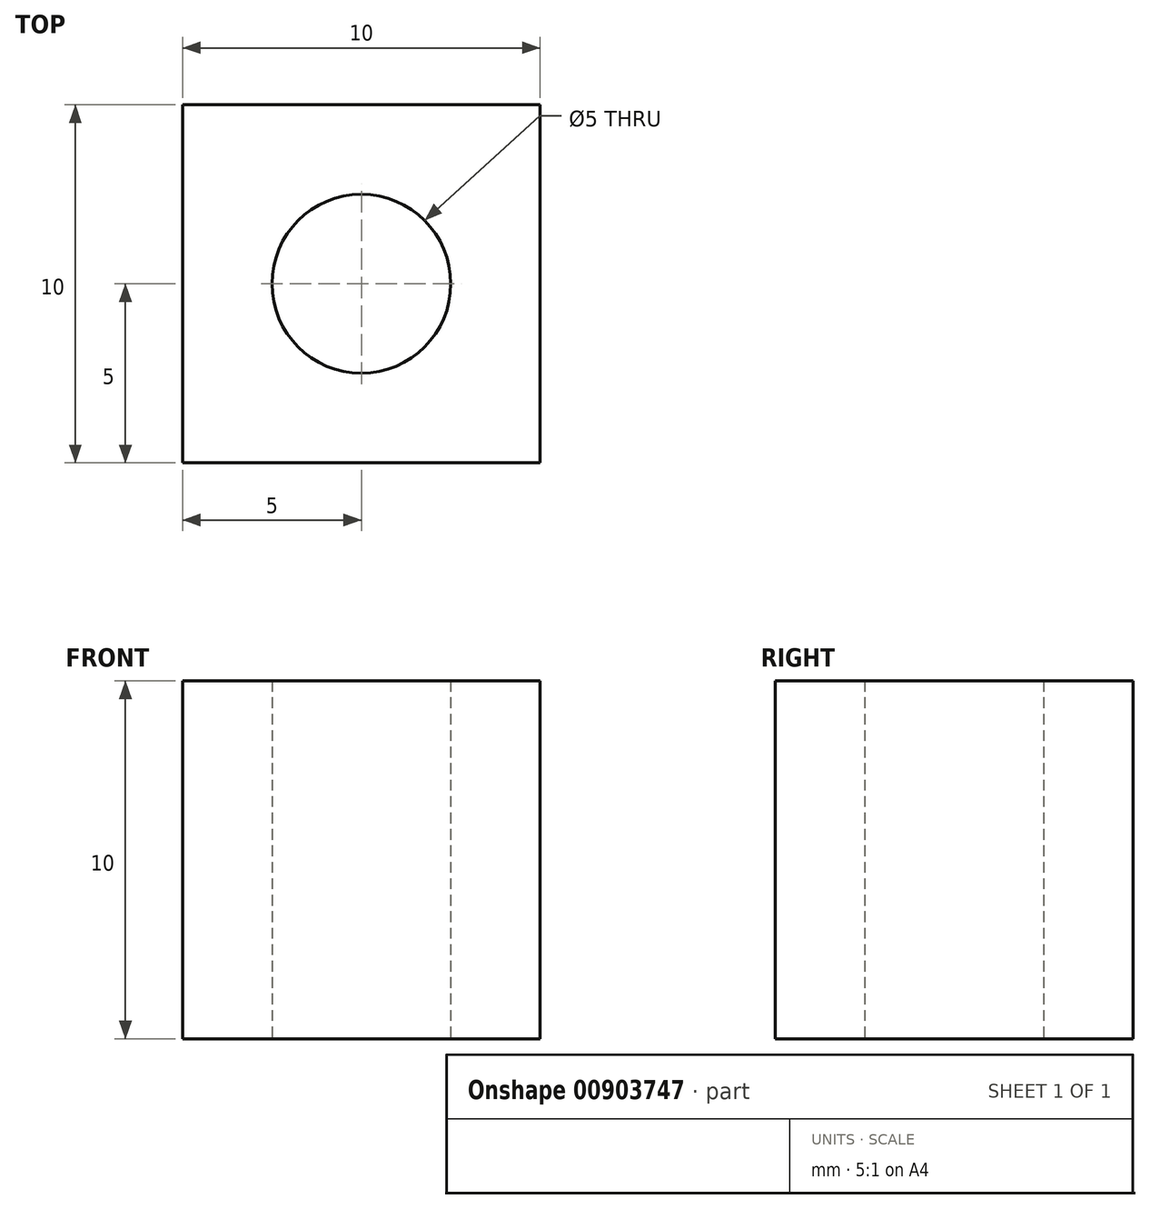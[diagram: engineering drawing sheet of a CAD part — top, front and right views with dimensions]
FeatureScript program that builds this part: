
annotation { "Feature Type Name" : "Feature", "Feature Type Description" : "" }
export const myFeature = defineFeature(function(context is Context, id is Id, definition is map)
    precondition{}
    {
        {
            var Q0;
            Q0=qCreatedBy(makeId("Top.planeOp"),FACE);
            var sketch = newSketch(context, id + "F0", { "sketchPlane" : qUnion([Q0])});
            skLineSegment(sketch, "E0.bottom", {"start": v(5, 5) * mm, "end": v(-5, 5) * mm});
            skLineSegment(sketch, "E0.top", {"start": v(5, -5) * mm, "end": v(-5, -5) * mm});
            skLineSegment(sketch, "E0.left", {"start": v(5, 5) * mm, "end": v(5, -5) * mm});
            skLineSegment(sketch, "E0.right", {"start": v(-5, 5) * mm, "end": v(-5, -5) * mm});
            skPoint(sketch, "E0.middle", {"position": v(0, 0) * mm});
            skCircle(sketch, "E1", {"center": v(0, 0) * mm, "radius": 2.5 * mm});
            skSolve(sketch);
        }
        {
            var Q0;
            Q0=makeQuery(id+"F0.imprint","IMPRINT",FACE,{"disambiguationData":[TD([[makeQuery(id+"F0.imprint","IMPRINT",EDGE,{"derivedFrom":sQuery(id+"F0.wireOp",EDGE,"E0.bottom")}),1.0]])]});
            extrude(context, id + "F1", {"entities" : qUnion([Q0]), "depth" : 10 * mm, "offsetDistance" : 25.4 * mm});
        }
    });
